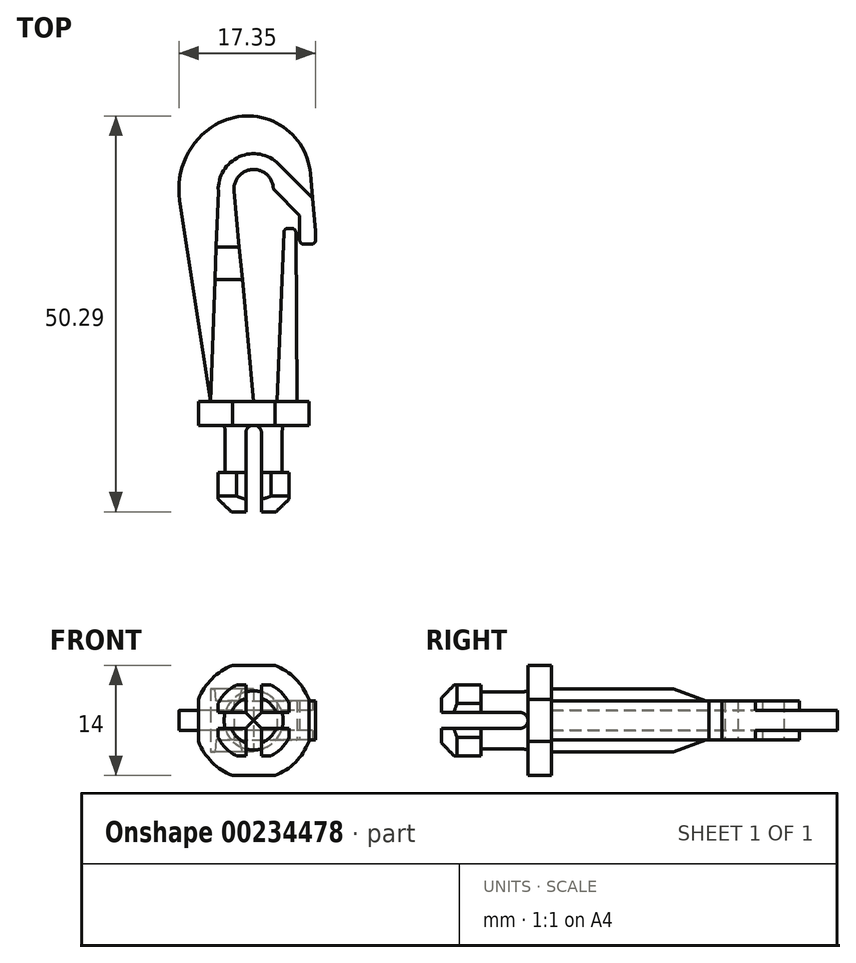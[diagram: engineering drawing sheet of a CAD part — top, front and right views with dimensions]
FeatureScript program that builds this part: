
annotation { "Feature Type Name" : "Feature", "Feature Type Description" : "" }
export const myFeature = defineFeature(function(context is Context, id is Id, definition is map)
    precondition{}
    {
        {
            var Q0;
            Q0=qCreatedBy(makeId("Top.planeOp"),FACE);
            var sketch = newSketch(context, id + "F0", { "sketchPlane" : qUnion([Q0])});
            skArc(sketch, "E0", {"start": v(2.5, 27) * mm, "mid": v(-0.12, 29.5) * mm, "end": v(-2.49, 26.77) * mm});
            skLineSegment(sketch, "E1", {"start": v(0, 0) * mm, "end": v(-2.49, 26.77) * mm});
            skLineSegment(sketch, "E2", {"start": v(0, 0) * mm, "end": v(-5.5, 0) * mm});
            skLineSegment(sketch, "E3", {"start": v(-5.5, 0) * mm, "end": v(-9.4, 25.57) * mm});
            skArc(sketch, "E4", {"start": v(6.8, 33.63) * mm, "mid": v(-4.23, 35.5) * mm, "end": v(-9.4, 25.57) * mm});
            skLineSegment(sketch, "E5", {"start": v(2.5, 27) * mm, "end": v(7.85, 21.65) * mm});
            skLineSegment(sketch, "E6", {"start": v(7.85, 21.65) * mm, "end": v(6.8, 33.63) * mm});
            skSolve(sketch);
        }
        {
            var Q0;
            Q0 = qSketchRegion(id + "F0", true);
            extrude(context, id + "F1", {"entities" : qUnion([Q0]), "depth" : 2.5 * mm, "offsetDistance" : 25 * mm, "symmetric" : true});
        }
        {
            var Q0;
            Q0=qCreatedBy(makeId("Top.planeOp"),FACE);
            var sketch = newSketch(context, id + "F2", { "sketchPlane" : qUnion([Q0])});
            skLineSegment(sketch, "E7.0", {"start": v(0, 0) * mm, "end": v(-2.49, 26.77) * mm});
            skLineSegment(sketch, "E8.0", {"start": v(0, 0) * mm, "end": v(-5.5, 0) * mm});
            skLineSegment(sketch, "E9", {"start": v(-5.5, 0) * mm, "end": v(-4.49, 26.77) * mm});
            skLineSegment(sketch, "E10", {"start": v(-4.49, 26.77) * mm, "end": v(-2.49, 26.77) * mm});
            skArc(sketch, "E11.0", {"start": v(2.5, 27) * mm, "mid": v(-0.12, 29.5) * mm, "end": v(-2.49, 26.77) * mm});
            skLineSegment(sketch, "E12.0", {"start": v(2.5, 27) * mm, "end": v(7.85, 21.65) * mm});
            skArc(sketch, "E13", {"start": v(-4.49, 26.77) * mm, "mid": v(-1.83, 31.1) * mm, "end": v(3.18, 30.18) * mm});
            skLineSegment(sketch, "E14", {"start": v(3.18, 30.18) * mm, "end": v(7.48, 25.88) * mm});
            skLineSegment(sketch, "E15", {"start": v(5.85, 23.65) * mm, "end": v(5.85, 20) * mm});
            skLineSegment(sketch, "E16", {"start": v(5.85, 20) * mm, "end": v(7.85, 20) * mm});
            skLineSegment(sketch, "E17.0", {"start": v(7.85, 21.65) * mm, "end": v(7.48, 25.88) * mm});
            skLineSegment(sketch, "E18", {"start": v(7.85, 21.65) * mm, "end": v(7.85, 20) * mm});
            skPoint(sketch, "E19.orphan", {"position": v(6.8, 33.63) * mm});
            skSolve(sketch);
        }
        {
            var Q0;
            Q0 = qSketchRegion(id + "F2", true);
            extrude(context, id + "F3", {"entities" : qUnion([Q0]), "operationType" : NewBodyOperationType.ADD, "depth" : 8 * mm, "offsetDistance" : 25 * mm, "symmetric" : true});
        }
        {
            var Q0;
            Q0=qCreatedBy(makeId("Front.planeOp"),FACE);
            var sketch = newSketch(context, id + "F4", { "sketchPlane" : qUnion([Q0])});
            skCircle(sketch, "E20", {"center": v(0, 0) * mm, "radius": 7.5 * mm});
            skSolve(sketch);
        }
        {
            var Q0;
            Q0 = qSketchRegion(id + "F4", true);
            extrude(context, id + "F5", {"entities" : qUnion([Q0]), "operationType" : NewBodyOperationType.ADD, "depth" : 3 * mm, "offsetDistance" : 25 * mm});
        }
        {
            var Q0;
            Q0=qCreatedBy(makeId("Top.planeOp"),FACE);
            var sketch = newSketch(context, id + "F6", { "sketchPlane" : qUnion([Q0])});
            skLineSegment(sketch, "E21", {"start": v(3, 0) * mm, "end": v(3.85, 22) * mm});
            skLineSegment(sketch, "E22", {"start": v(3.85, 22) * mm, "end": v(5.35, 22) * mm});
            skLineSegment(sketch, "E23", {"start": v(5.35, 22) * mm, "end": v(5.5, 0) * mm});
            skLineSegment(sketch, "E24", {"start": v(5.5, 0) * mm, "end": v(3, 0) * mm});
            skPoint(sketch, "E25.0", {"position": v(-5.5, 0) * mm});
            skSolve(sketch);
        }
        {
            var Q0;
            Q0 = qSketchRegion(id + "F6", true);
            extrude(context, id + "F7", {"entities" : qUnion([Q0]), "operationType" : NewBodyOperationType.ADD, "depth" : 5 * mm, "offsetDistance" : 25 * mm, "symmetric" : true});
        }
        {
            var Q0;
            Q0=qCreatedBy(makeId("Right.planeOp"),FACE);
            var sketch = newSketch(context, id + "F8", { "sketchPlane" : qUnion([Q0])});
            skLineSegment(sketch, "E26", {"start": v(31.5, 4) * mm, "end": v(31.5, 2.5) * mm});
            skLineSegment(sketch, "E27.0", {"start": v(26.77, 4) * mm, "end": v(31.5, 4) * mm});
            skLineSegment(sketch, "E28.0", {"start": v(15.5, 4) * mm, "end": v(26.77, 4) * mm});
            skLineSegment(sketch, "E29", {"start": v(31.5, 2.5) * mm, "end": v(19.62, 2.5) * mm});
            skLineSegment(sketch, "E30", {"start": v(19.62, 2.5) * mm, "end": v(15.5, 4) * mm});
            skPoint(sketch, "E31.orphan", {"position": v(0, 4) * mm});
            skLineSegment(sketch, "E32.MirrorCS", {"start": v(31.5, -4) * mm, "end": v(31.5, -2.5) * mm});
            skLineSegment(sketch, "E33.MirrorCS", {"start": v(31.5, -2.5) * mm, "end": v(19.62, -2.5) * mm});
            skLineSegment(sketch, "E34.MirrorCS", {"start": v(19.62, -2.5) * mm, "end": v(15.5, -4) * mm});
            skLineSegment(sketch, "E35.MirrorCS", {"start": v(26.77, -4) * mm, "end": v(31.5, -4) * mm});
            skLineSegment(sketch, "E36.MirrorCS", {"start": v(15.5, -4) * mm, "end": v(26.77, -4) * mm});
            skSolve(sketch);
        }
        {
            var Q0;
            Q0 = qSketchRegion(id + "F8", true);
            extrude(context, id + "F9", {"entities" : qUnion([Q0]), "operationType" : NewBodyOperationType.REMOVE, "depth" : 25 * mm, "offsetDistance" : 25 * mm, "symmetric" : true});
        }
        {
            var Q0;
            Q0=makeQuery(id+"F5.opExtrude","CAP_FACE",FACE,{"disambiguationData":[OSD([sQuery(id+"F4.wireOp",EDGE,"E20")])],"isStart":false});
            var sketch = newSketch(context, id + "F10", { "sketchPlane" : qUnion([Q0])});
            skCircle(sketch, "E37", {"center": v(0, 0) * mm, "radius": 3.75 * mm});
            skSolve(sketch);
        }
        {
            var Q0;
            Q0 = qSketchRegion(id + "F10", true);
            extrude(context, id + "F11", {"entities" : qUnion([Q0]), "operationType" : NewBodyOperationType.ADD, "depth" : 6 * mm, "offsetDistance" : 25 * mm});
        }
        {
            var Q0;
            Q0=makeQuery(id+"F11.opExtrude","CAP_FACE",FACE,{"disambiguationData":[OSD([sQuery(id+"F10.wireOp",EDGE,"E37")])],"isStart":false});
            var sketch = newSketch(context, id + "F12", { "sketchPlane" : qUnion([Q0])});
            skCircle(sketch, "E38", {"center": v(0, 0) * mm, "radius": 5 * mm});
            skSolve(sketch);
        }
        {
            var Q0;
            Q0 = qSketchRegion(id + "F12", true);
            extrude(context, id + "F13", {"entities" : qUnion([Q0]), "operationType" : NewBodyOperationType.ADD, "depth" : 5 * mm, "offsetDistance" : 25 * mm});
        }
        {
            var Q0;
            Q0=makeQuery(id+"F13.opExtrude","CAP_EDGE",EDGE,{"disambiguationData":[OSD([sQuery(id+"F12.wireOp",EDGE,"E38")])],"isStart":false});
            chamfer(context, id + "F14", {"entities" : qUnion([Q0]), "width" : 2 * mm, "tangentPropagation" : true});
        }
        {
            var Q0;
            Q0=makeQuery(id+"F13.opExtrude","CAP_FACE",FACE,{"disambiguationData":[OSD([sQuery(id+"F12.wireOp",EDGE,"E38")])],"isStart":false});
            var sketch = newSketch(context, id + "F15", { "sketchPlane" : qUnion([Q0])});
            skLineSegment(sketch, "E39", {"start": v(1, 10) * mm, "end": v(1, 1) * mm});
            skLineSegment(sketch, "E40", {"start": v(1, 1) * mm, "end": v(10, 1) * mm});
            skLineSegment(sketch, "E41", {"start": v(1, 10) * mm, "end": v(-1, 10) * mm});
            skLineSegment(sketch, "E42", {"start": v(-1, 10) * mm, "end": v(-1, 1) * mm});
            skLineSegment(sketch, "E43", {"start": v(-1, 1) * mm, "end": v(-10, 1) * mm});
            skLineSegment(sketch, "E44", {"start": v(-10, 1) * mm, "end": v(-10, -1) * mm});
            skLineSegment(sketch, "E45", {"start": v(-10, -1) * mm, "end": v(-1, -1) * mm});
            skLineSegment(sketch, "E46", {"start": v(-1, -1) * mm, "end": v(-1, -10) * mm});
            skLineSegment(sketch, "E47", {"start": v(-1, -10) * mm, "end": v(1, -10) * mm});
            skLineSegment(sketch, "E48", {"start": v(1, -10) * mm, "end": v(1, -1) * mm});
            skLineSegment(sketch, "E49", {"start": v(1, -1) * mm, "end": v(10, -1) * mm});
            skLineSegment(sketch, "E50", {"start": v(10, -1) * mm, "end": v(10, 1) * mm});
            skSolve(sketch);
        }
        {
            var Q0;
            Q0 = qSketchRegion(id + "F15", true);
            var Q1;
            Q1=makeQuery(id+"F5.opExtrude","CAP_FACE",FACE,{"disambiguationData":[OSD([sQuery(id+"F4.wireOp",EDGE,"E20")])],"isStart":false});
            extrude(context, id + "F16", {"entities" : qUnion([Q0]), "operationType" : NewBodyOperationType.REMOVE, "endBound" : BoundingType.UP_TO_SURFACE, "oppositeDirection" : true, "depth" : 25 * mm, "endBoundEntityFace" : qUnion([Q1]), "offsetDistance" : 25 * mm});
        }
        {
            var Q0;
            Q0=makeQuery(id+"F1.opExtrude","SWEPT_EDGE",EDGE,{"disambiguationData":[OSD([sQuery(id+"F0.wireOp",EDGE,"E4"),sQuery(id+"F0.wireOp",EDGE,"E6")])]});
            fillet(context, id + "F17", {"entities" : qUnion([Q0]), "tangentPropagation" : true, "radius" : 8 * mm, "defaultsChanged" : true, "vertexSettings" : [], "allowEdgeOverflow" : false});
        }
        {
            var Q0;
            Q0=makeQuery(id+"F3.opExtrude","SWEPT_EDGE",EDGE,{"disambiguationData":[OSD([sQuery(id+"F2.wireOp",EDGE,"E15"),sQuery(id+"F2.wireOp",EDGE,"E16")])]});
            var Q1;
            Q1=makeQuery(id+"F3.opExtrude","SWEPT_EDGE",EDGE,{"disambiguationData":[OSD([sQuery(id+"F2.wireOp",EDGE,"E16"),sQuery(id+"F2.wireOp",EDGE,"E18")])]});
            var Q2;
            Q2=makeQuery(id+"F7.opExtrude","SWEPT_EDGE",EDGE,{"disambiguationData":[OSD([sQuery(id+"F6.wireOp",EDGE,"E22"),sQuery(id+"F6.wireOp",EDGE,"E23")])]});
            var Q3;
            Q3=makeQuery(id+"F7.opExtrude","SWEPT_EDGE",EDGE,{"disambiguationData":[OSD([sQuery(id+"F6.wireOp",EDGE,"E21"),sQuery(id+"F6.wireOp",EDGE,"E22")])]});
            var Q4;
            Q4=makeQuery(id+"F3.boolean.opBoolean","MERGE",EDGE,{"derivedFrom":[makeQuery(id+"F1.opExtrude","SWEPT_EDGE",EDGE,{"disambiguationData":[OSD([sQuery(id+"F0.wireOp",EDGE,"E0"),sQuery(id+"F0.wireOp",EDGE,"E5")])]}),makeQuery(id+"F3.opExtrude","SWEPT_EDGE",EDGE,{"disambiguationData":[OSD([sQuery(id+"F2.wireOp",EDGE,"E11.0"),sQuery(id+"F2.wireOp",EDGE,"E12.0")])]})]});
            var Q5;
            Q5=makeQuery(id+"F3.boolean.opBoolean","MERGE",EDGE,{"derivedFrom":[makeQuery(id+"F1.opExtrude","SWEPT_EDGE",EDGE,{"disambiguationData":[OSD([sQuery(id+"F0.wireOp",EDGE,"E1"),sQuery(id+"F0.wireOp",EDGE,"E2")])]}),makeQuery(id+"F3.opExtrude","SWEPT_EDGE",EDGE,{"disambiguationData":[OSD([sQuery(id+"F2.wireOp",EDGE,"E7.0"),sQuery(id+"F2.wireOp",EDGE,"E8.0")])]})]});
            var Q6;
            Q6=makeQuery(id+"F7.opExtrude","SWEPT_EDGE",EDGE,{"disambiguationData":[OSD([sQuery(id+"F6.wireOp",EDGE,"E23"),sQuery(id+"F6.wireOp",EDGE,"E24")])]});
            var Q7;
            Q7=makeQuery(id+"F7.opExtrude","SWEPT_EDGE",EDGE,{"disambiguationData":[OSD([sQuery(id+"F6.wireOp",EDGE,"E21"),sQuery(id+"F6.wireOp",EDGE,"E24")])]});
            var Q8;
            Q8=makeQuery(id+"F1.opExtrude","SWEPT_EDGE",EDGE,{"disambiguationData":[OSD([sQuery(id+"F0.wireOp",EDGE,"E2"),sQuery(id+"F0.wireOp",EDGE,"E3")])]});
            fillet(context, id + "F18", {"entities" : qUnion([Q0, Q1, Q2, Q3, Q4, Q5, Q6, Q7, Q8]), "tangentPropagation" : true, "radius" : 0.5 * mm, "defaultsChanged" : false, "vertexSettings" : [], "allowEdgeOverflow" : false});
        }
        {
            var Q0;
            Q0=makeQuery(id+"F16.boolean.opBoolean","MERGE",FACE,{"derivedFrom":[makeQuery(id+"F5.opExtrude","CAP_FACE",FACE,{"disambiguationData":[OSD([sQuery(id+"F4.wireOp",EDGE,"E20")])],"isStart":false})],"fromTools":[makeQuery(id+"F16.opExtrude","CAP_FACE",FACE,{"disambiguationData":[OSD([sQuery(id+"F15.wireOp",EDGE,"E39"),sQuery(id+"F15.wireOp",EDGE,"E40"),sQuery(id+"F15.wireOp",EDGE,"E41"),sQuery(id+"F15.wireOp",EDGE,"E42"),sQuery(id+"F15.wireOp",EDGE,"E43"),sQuery(id+"F15.wireOp",EDGE,"E44"),sQuery(id+"F15.wireOp",EDGE,"E45"),sQuery(id+"F15.wireOp",EDGE,"E46"),sQuery(id+"F15.wireOp",EDGE,"E47"),sQuery(id+"F15.wireOp",EDGE,"E48"),sQuery(id+"F15.wireOp",EDGE,"E49"),sQuery(id+"F15.wireOp",EDGE,"E50")])],"isStart":false})]});
            var sketch = newSketch(context, id + "F19", { "sketchPlane" : qUnion([Q0])});
            skLineSegment(sketch, "E51.bottom", {"start": v(-4.5, 4.5) * mm, "end": v(4.5, 4.5) * mm});
            skLineSegment(sketch, "E51.top", {"start": v(-4.5, -4.5) * mm, "end": v(4.5, -4.5) * mm});
            skLineSegment(sketch, "E51.left", {"start": v(-4.5, 4.5) * mm, "end": v(-4.5, -4.5) * mm});
            skLineSegment(sketch, "E51.right", {"start": v(4.5, 4.5) * mm, "end": v(4.5, -4.5) * mm});
            skPoint(sketch, "E51.middle", {"position": v(0, 0) * mm});
            skLineSegment(sketch, "E52.bottom", {"start": v(-10, 10) * mm, "end": v(10, 10) * mm});
            skLineSegment(sketch, "E52.top", {"start": v(-10, -10) * mm, "end": v(10, -10) * mm});
            skLineSegment(sketch, "E52.left", {"start": v(-10, 10) * mm, "end": v(-10, -10) * mm});
            skLineSegment(sketch, "E52.right", {"start": v(10, 10) * mm, "end": v(10, -10) * mm});
            skSolve(sketch);
        }
        {
            var Q0;
            Q0 = qSketchRegion(id + "F19", true);
            extrude(context, id + "F20", {"entities" : qUnion([Q0]), "operationType" : NewBodyOperationType.REMOVE, "endBound" : BoundingType.THROUGH_ALL, "depth" : 25 * mm, "offsetDistance" : 25 * mm});
        }
        {
            var Q0;
            {var subQ0=sQuery(id+"F15.wireOp",EDGE,"E45");var subQ1=sQuery(id+"F10.wireOp",EDGE,"E37");Q0=makeQuery(id+"F16.boolean.opBoolean","SPLIT",EDGE,{"disambiguationData":[TD([makeQuery(id+"F16.opExtrude","SWEPT_FACE",FACE,{"disambiguationData":[OSD([subQ0])]})])],"derivedFrom":makeQuery(id+"F11.opExtrude","CAP_EDGE",EDGE,{"disambiguationData":[OSD([subQ1])],"isStart":true})});}
            var Q1;
            {var subQ1=sQuery(id+"F15.wireOp",EDGE,"E48");var subQ2=sQuery(id+"F10.wireOp",EDGE,"E37");Q1=makeQuery(id+"F16.boolean.opBoolean","SPLIT",EDGE,{"disambiguationData":[TD([makeQuery(id+"F16.opExtrude","SWEPT_FACE",FACE,{"disambiguationData":[OSD([subQ1])]})])],"derivedFrom":makeQuery(id+"F11.opExtrude","CAP_EDGE",EDGE,{"disambiguationData":[OSD([subQ2])],"isStart":true})});}
            var Q2;
            {var subQ1=sQuery(id+"F15.wireOp",EDGE,"E39");var subQ2=sQuery(id+"F10.wireOp",EDGE,"E37");Q2=makeQuery(id+"F16.boolean.opBoolean","SPLIT",EDGE,{"disambiguationData":[TD([makeQuery(id+"F16.opExtrude","SWEPT_FACE",FACE,{"disambiguationData":[OSD([subQ1])]})])],"derivedFrom":makeQuery(id+"F11.opExtrude","CAP_EDGE",EDGE,{"disambiguationData":[OSD([subQ2])],"isStart":true})});}
            var Q3;
            {var subQ0=sQuery(id+"F15.wireOp",EDGE,"E42");var subQ2=sQuery(id+"F10.wireOp",EDGE,"E37");Q3=makeQuery(id+"F16.boolean.opBoolean","SPLIT",EDGE,{"disambiguationData":[TD([makeQuery(id+"F16.opExtrude","SWEPT_FACE",FACE,{"disambiguationData":[OSD([subQ0])]})])],"derivedFrom":makeQuery(id+"F11.opExtrude","CAP_EDGE",EDGE,{"disambiguationData":[OSD([subQ2])],"isStart":true})});}
            var Q4;
            Q4=makeQuery(id+"F16.boolean.opBoolean","COPY",EDGE,{"derivedFrom":makeQuery(id+"F16.opExtrude","CAP_EDGE",EDGE,{"disambiguationData":[OSD([sQuery(id+"F15.wireOp",EDGE,"E42")])],"isStart":false})});
            var Q5;
            Q5=makeQuery(id+"F16.boolean.opBoolean","COPY",EDGE,{"derivedFrom":makeQuery(id+"F16.opExtrude","CAP_EDGE",EDGE,{"disambiguationData":[OSD([sQuery(id+"F15.wireOp",EDGE,"E39")])],"isStart":false})});
            var Q6;
            Q6=makeQuery(id+"F16.boolean.opBoolean","COPY",EDGE,{"derivedFrom":makeQuery(id+"F16.opExtrude","CAP_EDGE",EDGE,{"disambiguationData":[OSD([sQuery(id+"F15.wireOp",EDGE,"E40")])],"isStart":false})});
            var Q7;
            Q7=makeQuery(id+"F16.boolean.opBoolean","COPY",EDGE,{"derivedFrom":makeQuery(id+"F16.opExtrude","CAP_EDGE",EDGE,{"disambiguationData":[OSD([sQuery(id+"F15.wireOp",EDGE,"E43")])],"isStart":false})});
            var Q8;
            Q8=makeQuery(id+"F16.boolean.opBoolean","COPY",EDGE,{"derivedFrom":makeQuery(id+"F16.opExtrude","CAP_EDGE",EDGE,{"disambiguationData":[OSD([sQuery(id+"F15.wireOp",EDGE,"E45")])],"isStart":false})});
            var Q9;
            Q9=makeQuery(id+"F16.boolean.opBoolean","COPY",EDGE,{"derivedFrom":makeQuery(id+"F16.opExtrude","CAP_EDGE",EDGE,{"disambiguationData":[OSD([sQuery(id+"F15.wireOp",EDGE,"E49")])],"isStart":false})});
            var Q10;
            Q10=makeQuery(id+"F16.boolean.opBoolean","COPY",EDGE,{"derivedFrom":makeQuery(id+"F16.opExtrude","CAP_EDGE",EDGE,{"disambiguationData":[OSD([sQuery(id+"F15.wireOp",EDGE,"E46")])],"isStart":false})});
            var Q11;
            Q11=makeQuery(id+"F16.boolean.opBoolean","COPY",EDGE,{"derivedFrom":makeQuery(id+"F16.opExtrude","CAP_EDGE",EDGE,{"disambiguationData":[OSD([sQuery(id+"F15.wireOp",EDGE,"E48")])],"isStart":false})});
            fillet(context, id + "F21", {"entities" : qUnion([Q0, Q1, Q2, Q3, Q4, Q5, Q6, Q7, Q8, Q9, Q10, Q11]), "tangentPropagation" : true, "radius" : 1 * mm, "defaultsChanged" : true, "vertexSettings" : [], "allowEdgeOverflow" : false});
        }
        {
            var Q0;
            Q0=qCreatedBy(makeId("Front.planeOp"),FACE);
            var sketch = newSketch(context, id + "F22", { "sketchPlane" : qUnion([Q0])});
            skLineSegment(sketch, "E53.bottom", {"start": v(-7, 7) * mm, "end": v(7, 7) * mm});
            skLineSegment(sketch, "E53.top", {"start": v(-7, -7) * mm, "end": v(7, -7) * mm});
            skLineSegment(sketch, "E53.left", {"start": v(-7, 7) * mm, "end": v(-7, -7) * mm});
            skLineSegment(sketch, "E53.right", {"start": v(7, 7) * mm, "end": v(7, -7) * mm});
            skPoint(sketch, "E53.middle", {"position": v(0, 0) * mm});
            skLineSegment(sketch, "E54.bottom", {"start": v(-10, 10) * mm, "end": v(10, 10) * mm});
            skLineSegment(sketch, "E54.top", {"start": v(-10, -10) * mm, "end": v(10, -10) * mm});
            skLineSegment(sketch, "E54.left", {"start": v(-10, 10) * mm, "end": v(-10, -10) * mm});
            skLineSegment(sketch, "E54.right", {"start": v(10, 10) * mm, "end": v(10, -10) * mm});
            skSolve(sketch);
        }
        {
            var Q0;
            Q0 = qSketchRegion(id + "F22", true);
            var Q1;
            Q1=makeQuery(id+"F16.boolean.opBoolean","MERGE",FACE,{"derivedFrom":[makeQuery(id+"F5.opExtrude","CAP_FACE",FACE,{"disambiguationData":[OSD([sQuery(id+"F4.wireOp",EDGE,"E20")])],"isStart":false})],"fromTools":[makeQuery(id+"F16.opExtrude","CAP_FACE",FACE,{"disambiguationData":[OSD([sQuery(id+"F15.wireOp",EDGE,"E39"),sQuery(id+"F15.wireOp",EDGE,"E40"),sQuery(id+"F15.wireOp",EDGE,"E41"),sQuery(id+"F15.wireOp",EDGE,"E42"),sQuery(id+"F15.wireOp",EDGE,"E43"),sQuery(id+"F15.wireOp",EDGE,"E44"),sQuery(id+"F15.wireOp",EDGE,"E45"),sQuery(id+"F15.wireOp",EDGE,"E46"),sQuery(id+"F15.wireOp",EDGE,"E47"),sQuery(id+"F15.wireOp",EDGE,"E48"),sQuery(id+"F15.wireOp",EDGE,"E49"),sQuery(id+"F15.wireOp",EDGE,"E50")])],"isStart":false})]});
            extrude(context, id + "F23", {"entities" : qUnion([Q0]), "operationType" : NewBodyOperationType.REMOVE, "endBound" : BoundingType.UP_TO_SURFACE, "depth" : 25 * mm, "endBoundEntityFace" : qUnion([Q1]), "offsetDistance" : 25 * mm});
        }
    });
